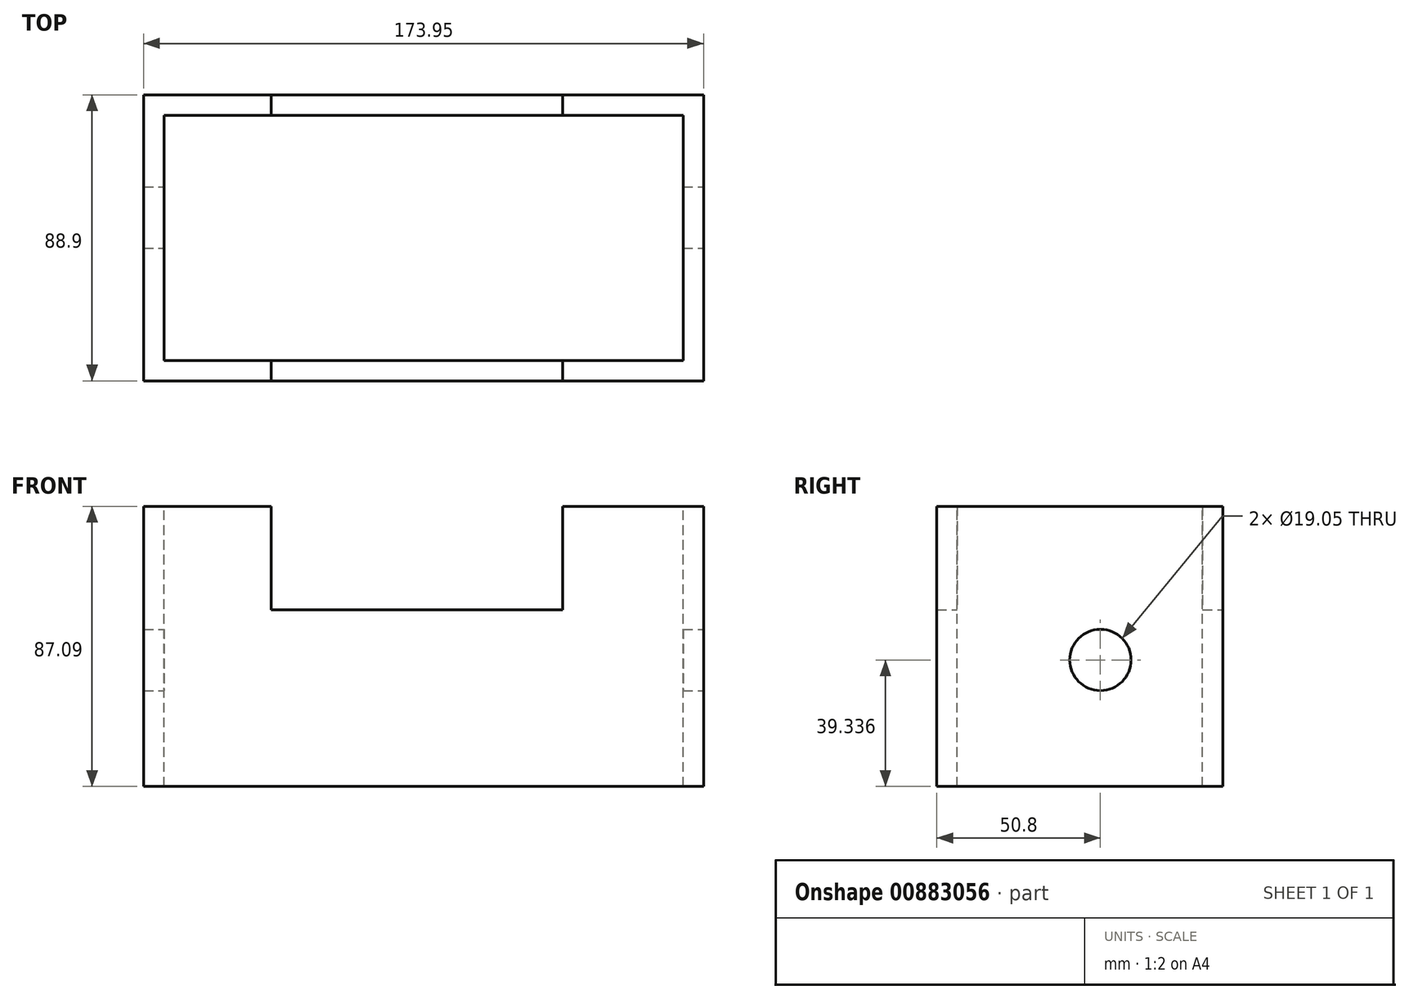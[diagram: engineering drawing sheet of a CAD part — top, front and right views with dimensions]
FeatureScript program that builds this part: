
annotation { "Feature Type Name" : "Feature", "Feature Type Description" : "" }
export const myFeature = defineFeature(function(context is Context, id is Id, definition is map)
    precondition{}
    {
        {
            var Q0;
            Q0=qCreatedBy(makeId("Front.planeOp"),FACE);
            var sketch = newSketch(context, id + "F0", { "sketchPlane" : qUnion([Q0])});
            skLineSegment(sketch, "E0.bottom", {"start": v(-110.05, -58.13) * mm, "end": v(63.9, -58.13) * mm});
            skLineSegment(sketch, "E0.top", {"start": v(-110.05, 28.96) * mm, "end": v(-70.43, 28.96) * mm});
            skLineSegment(sketch, "E0.left", {"start": v(-110.05, -58.13) * mm, "end": v(-110.05, 28.96) * mm});
            skLineSegment(sketch, "E0.right", {"start": v(63.9, -58.13) * mm, "end": v(63.9, 28.96) * mm});
            skLineSegment(sketch, "E1.top", {"start": v(-70.43, -3.27) * mm, "end": v(20.14, -3.27) * mm});
            skLineSegment(sketch, "E1.left", {"start": v(-70.43, 28.96) * mm, "end": v(-70.43, -3.27) * mm});
            skLineSegment(sketch, "E1.right", {"start": v(20.14, 28.96) * mm, "end": v(20.14, -3.27) * mm});
            skLineSegment(sketch, "E2.trimOffspring", {"start": v(20.14, 28.96) * mm, "end": v(63.9, 28.96) * mm});
            skSolve(sketch);
        }
        {
            var Q0;
            Q0=makeQuery(id+"F0.imprint","IMPRINT",FACE,{"disambiguationData":[TD([[makeQuery(id+"F0.imprint","IMPRINT",EDGE,{"derivedFrom":sQuery(id+"F0.wireOp",EDGE,"E0.bottom")}),1.0]])]});
            extrude(context, id + "F1", {"entities" : qUnion([Q0]), "depth" : 50.8 * mm, "offsetDistance" : 25.4 * mm, "hasSecondDirection" : true, "secondDirectionOppositeDirection" : true, "secondDirectionDepth" : 38.1 * mm});
        }
        {
            var Q0;
            Q0=makeQuery(id+"F1.opExtrude","SWEPT_FACE",FACE,{"disambiguationData":[OSD([sQuery(id+"F0.wireOp",EDGE,"E0.top")])]});
            var Q1;
            Q1=makeQuery(id+"F1.opExtrude","SWEPT_FACE",FACE,{"disambiguationData":[OSD([sQuery(id+"F0.wireOp",EDGE,"E1.left")])]});
            var Q2;
            Q2=makeQuery(id+"F1.opExtrude","SWEPT_FACE",FACE,{"disambiguationData":[OSD([sQuery(id+"F0.wireOp",EDGE,"E1.right")])]});
            var Q3;
            Q3=makeQuery(id+"F1.opExtrude","SWEPT_FACE",FACE,{"disambiguationData":[OSD([sQuery(id+"F0.wireOp",EDGE,"E2.trimOffspring")])]});
            var Q4;
            Q4=makeQuery(id+"F1.opExtrude","SWEPT_FACE",FACE,{"disambiguationData":[OSD([sQuery(id+"F0.wireOp",EDGE,"E1.top")])]});
            var Q5;
            Q5=makeQuery(id+"F1.opExtrude","SWEPT_FACE",FACE,{"disambiguationData":[OSD([sQuery(id+"F0.wireOp",EDGE,"E0.bottom")])]});
            shell(context, id + "F2", {"entities" : qUnion([Q0, Q1, Q2, Q3, Q4, Q5]), "thickness" : 6.35 * mm});
        }
        {
            var Q0;
            Q0=makeQuery(id+"F1.opExtrude","SWEPT_FACE",FACE,{"disambiguationData":[OSD([sQuery(id+"F0.wireOp",EDGE,"E0.right")])]});
            var sketch = newSketch(context, id + "F3", { "sketchPlane" : qUnion([Q0])});
            skPoint(sketch, "E3", {"position": v(0, -18.8) * mm});
            skSolve(sketch);
        }
        {
            var Q0;
            Q0=sQuery(id+"F3.wireOp",VERTEX,"E3");
            var Q1;
            Q1=makeQuery(id+"F1.opExtrude","SWEPT_BODY",BODY,{"disambiguationData":[OSD([sQuery(id+"F0.wireOp",EDGE,"E0.bottom"),sQuery(id+"F0.wireOp",EDGE,"E0.top"),sQuery(id+"F0.wireOp",EDGE,"E0.left"),sQuery(id+"F0.wireOp",EDGE,"E0.right"),sQuery(id+"F0.wireOp",EDGE,"E1.top"),sQuery(id+"F0.wireOp",EDGE,"E1.left"),sQuery(id+"F0.wireOp",EDGE,"E1.right"),sQuery(id+"F0.wireOp",EDGE,"E2.trimOffspring")])]});
            hole(context, id + "F4", {"style" : HoleStyle.SIMPLE, "endStyle" : HoleEndStyle.THROUGH, "holeDiameter" : 19.05 * mm, "majorDiameter" : 6.35 * mm, "isTappedThrough" : true, "tappedDepth" : 12.7 * mm, "tapClearance" : 3, "locations" : qUnion([Q0]), "scope" : qUnion([Q1])});
        }
    });
